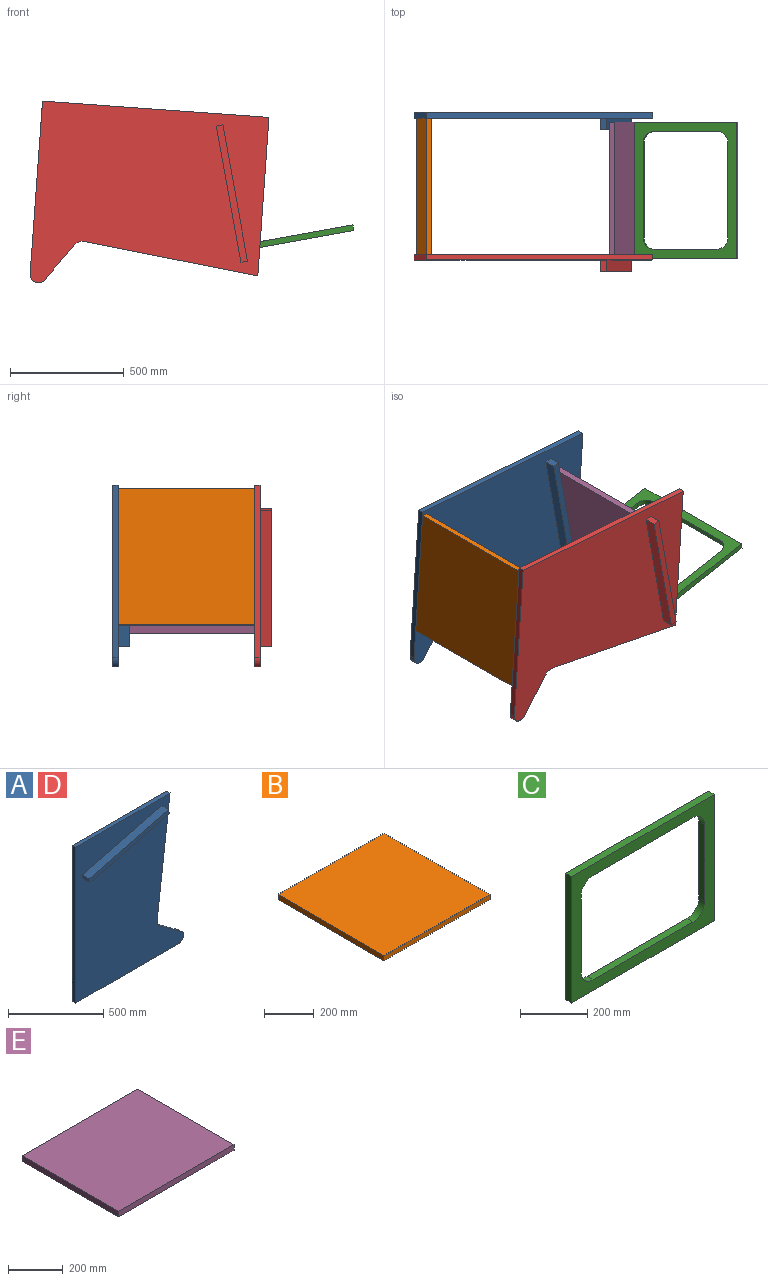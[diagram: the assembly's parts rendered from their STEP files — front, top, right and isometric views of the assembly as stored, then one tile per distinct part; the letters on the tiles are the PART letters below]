
ASSEMBLY  parts=5 mates=6
PART A: 14 faces, bbox 800x75x1001.2 mm
  f0: plane 700x25mm, normal (0,0,1), area 17500mm2, adj f1,f6,f7,f8
  f1: plane 1000x25mm, normal (-1,0,0), area 25000mm2, adj f0,f2,f7,f8
  f2: plane 762.75x25mm, normal (0,0,-1), area 19068.7mm2, adj f1,f3,f7,f8
  f3: cylinder r=37.25mm len=71.59mm, axis (0,1,0), area 2554.6mm2, adj f2,f4,f7,f8
  f4: plane 153.43x112.04mm, normal (0.59,0,0.81), area 4749.5mm2, adj f3,f5,f7,f8
  f5: cylinder r=50mm len=46.58mm, axis (0,1,0), area 1330.5mm2, adj f4,f6,f7,f8
  f6: plane 770.95x96.35mm, normal (0.99,0,-0.12), area 19423.7mm2, adj f0,f5,f7,f8
  f7: plane 1001.16x800mm, normal (0,-1,0), area 647792.6mm2, adj f0,f1,f2,f3,f4,f5,f6,f9
  f8: plane 1001.16x800mm, normal (0,1,0), area 665705.7mm2, adj f0,f1,f2,f3,f4,f5,f6
  f9: plane 590.05x150.97mm, normal (-0.25,0,0.97), area 30453mm2, adj f7,f10,f12,f13
  f10: plane 50x28.49mm, normal (-0.97,0,-0.25), area 1470.6mm2, adj f7,f9,f11,f13
  f11: plane 590.05x150.97mm, normal (0.25,0,-0.97), area 30453mm2, adj f7,f10,f12,f13
  f12: plane 50x28.49mm, normal (0.97,0,0.25), area 1470.6mm2, adj f7,f9,f11,f13
  f13: plane 597.34x179.47mm, normal (0,-1,0), area 17913.1mm2, adj f9,f10,f11,f12
PART B: 6 faces, bbox 600x600x25 mm
  f0: plane 600x25mm, normal (-1,0,0), area 15000mm2, adj f1,f3,f4,f5
  f1: plane 600x25mm, normal (0,-1,0), area 15000mm2, adj f0,f2,f4,f5
  f2: plane 600x25mm, normal (1,0,0), area 15000mm2, adj f1,f3,f4,f5
  f3: plane 600x25mm, normal (0,1,0), area 15000mm2, adj f0,f2,f4,f5
  f4: plane 600x600mm, normal (0,0,1), area 360000mm2, adj f0,f1,f2,f3
  f5: plane 600x600mm, normal (0,0,-1), area 360000mm2, adj f0,f1,f2,f3
PART C: 14 faces, bbox 600x25x460 mm
  f0: plane 600x25mm, normal (0,0,1), area 15000mm2, adj f1,f11,f12,f13
  f1: plane 460x25mm, normal (-1,0,0), area 11500mm2, adj f0,f2,f12,f13
  f2: plane 600x25mm, normal (0,0,-1), area 15000mm2, adj f1,f11,f12,f13
  f3: cylinder r=50mm len=50mm, axis (0,1,0), area 1963.5mm2, adj f4,f10,f12,f13
  f4: plane 420x25mm, normal (0,0,-1), area 10500mm2, adj f3,f5,f12,f13
  f5: cylinder r=50mm len=50mm, axis (0,1,0), area 1963.5mm2, adj f4,f6,f12,f13
  f6: plane 280x25mm, normal (-1,0,0), area 7000mm2, adj f5,f7,f12,f13
  f7: cylinder r=50mm len=50mm, axis (0,1,0), area 1963.5mm2, adj f6,f8,f12,f13
  f8: plane 420x25mm, normal (0,0,1), area 10500mm2, adj f7,f9,f12,f13
  f9: cylinder r=50mm len=50mm, axis (0,1,0), area 1963.5mm2, adj f8,f10,f12,f13
  f10: plane 280x25mm, normal (1,0,0), area 7000mm2, adj f3,f9,f12,f13
  f11: plane 460x25mm, normal (1,0,0), area 11500mm2, adj f0,f2,f12,f13
  f12: plane 600x460mm, normal (0,-1,0), area 80546mm2, adj f0,f1,f2,f3,f4,f5,f6,f7
  f13: plane 600x460mm, normal (0,1,0), area 80546mm2, adj f0,f1,f2,f3,f4,f5,f6,f7
PART D: same geometry as A
PART E: 6 faces, bbox 600x500x25 mm
  f0: plane 600x25mm, normal (0,1,0), area 15000mm2, adj f1,f3,f4,f5
  f1: plane 500x25mm, normal (-1,0,0), area 12500mm2, adj f0,f2,f4,f5
  f2: plane 600x25mm, normal (0,-1,0), area 15000mm2, adj f1,f3,f4,f5
  f3: plane 500x25mm, normal (1,0,0), area 12500mm2, adj f0,f2,f4,f5
  f4: plane 600x500mm, normal (0,0,1), area 300000mm2, adj f0,f1,f2,f3
  f5: plane 600x500mm, normal (0,0,-1), area 300000mm2, adj f0,f1,f2,f3
PLACE A rot(axis=(0,1,0),94.1deg) t=(-78.04,-24.84,-419.67)mm
PLACE B rot(axis=(0,1,0),94.1deg) t=(-688.32,-410.7,-603.1)mm
PLACE C rot(axis=(-0.61,-0.61,0.51),126.1deg) t=(731.41,-342.48,-839)mm
PLACE D rot(axis=(0,1,0),94.1deg) t=(-78.04,-649.84,-419.67)mm
PLACE E rot(axis=(-0.61,-0.61,0.51),126.1deg) t=(211.63,-392.33,-690.09)mm
MATE planar B.f3 <-> A.f7  axis (0,1,0) through (-662.39,-49.84,-591.08)mm
MATE planar D.f2 <-> B.f5  axis (-1,0,0.07) through (-691.98,-662.34,-654.06)mm
MATE planar E.f4 <-> A.f9  axis (-0.98,0,-0.18) through (184.62,-366.88,-681.26)mm
MATE planar C.f0 <-> E.f5  axis (-0.98,0,-0.18) through (251.92,-366.88,-912.98)mm
MATE planar D.f8 <-> B.f1  axis (0,1,0) through (-191.92,-649.84,-643)mm
MATE planar D.f2 <-> A.f2  axis (-1,0,0.07) through (-691.98,-662.34,-654.06)mm
